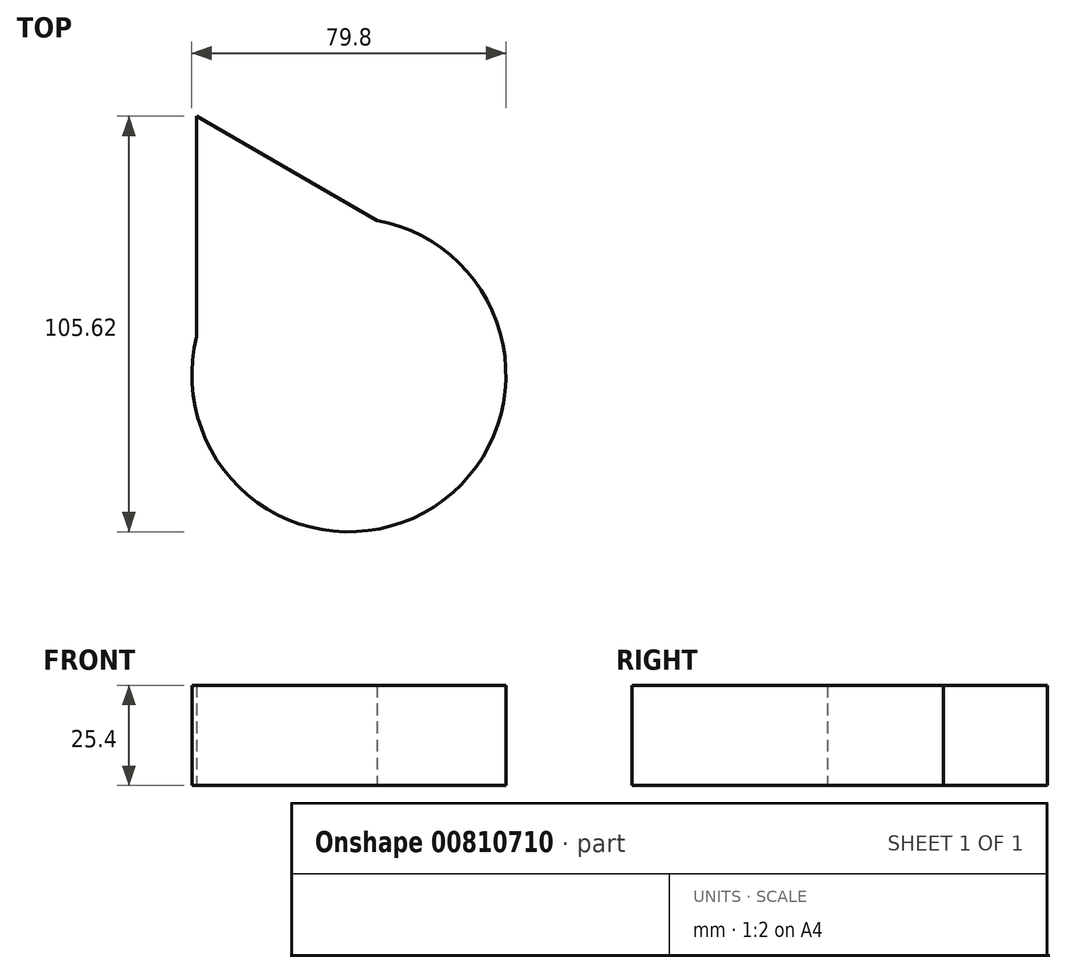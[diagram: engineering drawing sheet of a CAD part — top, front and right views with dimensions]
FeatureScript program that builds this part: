
annotation { "Feature Type Name" : "Feature", "Feature Type Description" : "" }
export const myFeature = defineFeature(function(context is Context, id is Id, definition is map)
    precondition{}
    {
        {
            var Q0;
            Q0=qCreatedBy(makeId("Top.planeOp"),FACE);
            var sketch = newSketch(context, id + "F0", { "sketchPlane" : qUnion([Q0])});
            skArc(sketch, "E0", {"start": v(-45.85, 0) * mm, "mid": v(14.42, -43.3) * mm, "end": v(0, 29.5) * mm});
            skLineSegment(sketch, "E1", {"start": v(-45.85, 0) * mm, "end": v(-45.85, 55.97) * mm});
            skLineSegment(sketch, "E2", {"start": v(0, 29.5) * mm, "end": v(-45.85, 55.97) * mm});
            skSolve(sketch);
        }
        {
            var Q0;
            Q0=makeQuery(id+"F0.imprint","IMPRINT",FACE,{"disambiguationData":[TD([[makeQuery(id+"F0.imprint","IMPRINT",EDGE,{"derivedFrom":sQuery(id+"F0.wireOp",EDGE,"E0")}),1.0]])]});
            extrude(context, id + "F1", {"entities" : qUnion([Q0]), "depth" : 25.4 * mm, "offsetDistance" : 25.4 * mm});
        }
    });
